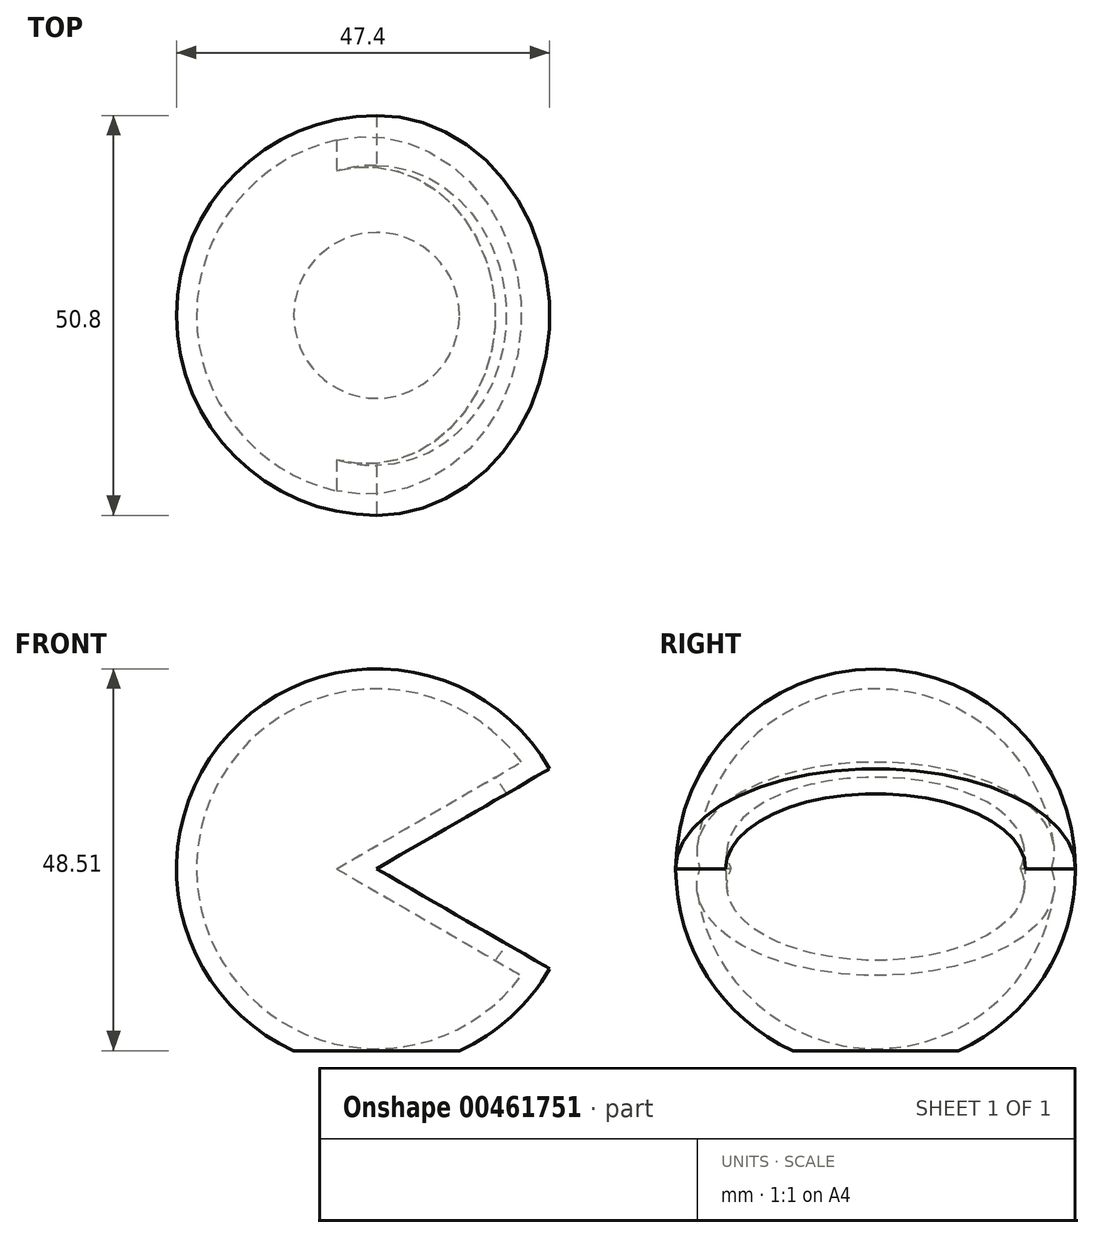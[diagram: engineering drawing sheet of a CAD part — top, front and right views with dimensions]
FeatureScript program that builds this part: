
annotation { "Feature Type Name" : "Feature", "Feature Type Description" : "" }
export const myFeature = defineFeature(function(context is Context, id is Id, definition is map)
    precondition{}
    {
        {
            var Q0;
            Q0=qCreatedBy(makeId("Top.planeOp"),FACE);
            var sketch = newSketch(context, id + "F0", { "sketchPlane" : qUnion([Q0])});
            skCircle(sketch, "E0", {"center": v(0, 0) * mm, "radius": 25.4 * mm});
            skLineSegment(sketch, "E1", {"start": v(0, 25.4) * mm, "end": v(0, -25.4) * mm});
            skSolve(sketch);
        }
        {
            var Q0;
            {var subQ0=sQuery(id+"F0.wireOp",EDGE,"E1");Q0=makeQuery(id+"F0.imprint","IMPRINT",FACE,{"disambiguationData":[TD([[makeQuery(id+"F0.imprint","IMPRINT",EDGE,{"derivedFrom":subQ0}),-1.0]])]});}
            var Q1;
            Q1=sQuery(id+"F0.wireOp",EDGE,"E1");
            revolve(context, id + "F1", {"entities" : qUnion([Q0]), "axis" : qUnion([Q1]), "revolveType" : RevolveType.SYMMETRIC, "oppositeDirection" : true, "angle" : 300 * degree});
        }
        {
            var Q0;
            Q0=makeQuery(id+"F1.opRevolve","SWEPT_FACE",FACE,{"disambiguationData":[OSD([sQuery(id+"F0.wireOp",EDGE,"E0")])]});
            var Q1;
            Q1=makeQuery(id+"F1.opRevolve","SWEPT_BODY",BODY,{"disambiguationData":[OSD([sQuery(id+"F0.wireOp",EDGE,"E0"),sQuery(id+"F0.wireOp",EDGE,"E1")])]});
            shell(context, id + "F2", {"isHollow" : true, "entities" : qUnion([Q0]), "parts" : qUnion([Q1]), "thickness" : 2.54 * mm});
        }
        {
            var Q0;
            Q0=makeQuery(id+"F1.opRevolve","CAP_FACE",FACE,{"disambiguationData":[OSD([sQuery(id+"F0.wireOp",EDGE,"E0"),sQuery(id+"F0.wireOp",EDGE,"E1")])],"isStart":true});
            var sketch = newSketch(context, id + "F3", { "sketchPlane" : qUnion([Q0])});
            skArc(sketch, "E2", {"start": v(0, -19.05) * mm, "mid": v(19.05, 0) * mm, "end": v(0, 19.05) * mm});
            skLineSegment(sketch, "E3", {"start": v(0, -19.05) * mm, "end": v(0, 19.05) * mm});
            skSolve(sketch);
        }
        {
            var Q0;
            Q0=makeQuery(id+"F3.imprint","IMPRINT",FACE,{"disambiguationData":[TD([[makeQuery(id+"F3.imprint","IMPRINT",EDGE,{"derivedFrom":sQuery(id+"F3.wireOp",EDGE,"E2")}),1.0]])]});
            var Q1;
            Q1=sQuery(id+"F3.wireOp",EDGE,"E3");
            revolve(context, id + "F4", {"operationType" : NewBodyOperationType.REMOVE, "entities" : qUnion([Q0]), "axis" : qUnion([Q1]), "revolveType" : RevolveType.FULL, "oppositeDirection" : true});
        }
        {
            var Q0;
            Q0=qCreatedBy(makeId("Top.planeOp"),FACE);
            cPlane(context, id + "F5", {"entities" : qUnion([Q0]), "cplaneType" : CPlaneType.OFFSET, "offset" : 25.4 * mm, "oppositeDirection" : true, "width" : 152.4 * mm, "height" : 152.4 * mm});
        }
        {
            var Q0;
            Q0=qCreatedBy(id+"F5.planeOp",FACE);
            var sketch = newSketch(context, id + "F6", { "sketchPlane" : qUnion([Q0])});
            skLineSegment(sketch, "E4.bottom", {"start": v(-31.75, -31.75) * mm, "end": v(31.75, -31.75) * mm});
            skLineSegment(sketch, "E4.top", {"start": v(-31.75, 31.75) * mm, "end": v(31.75, 31.75) * mm});
            skLineSegment(sketch, "E4.left", {"start": v(-31.75, -31.75) * mm, "end": v(-31.75, 31.75) * mm});
            skLineSegment(sketch, "E4.right", {"start": v(31.75, -31.75) * mm, "end": v(31.75, 31.75) * mm});
            skPoint(sketch, "E4.middle", {"position": v(0, 0) * mm});
            skSolve(sketch);
        }
        {
            var Q0;
            Q0 = qSketchRegion(id + "F6", true);
            extrude(context, id + "F7", {"entities" : qUnion([Q0]), "operationType" : NewBodyOperationType.REMOVE, "depth" : 2.3 * mm});
        }
    });
